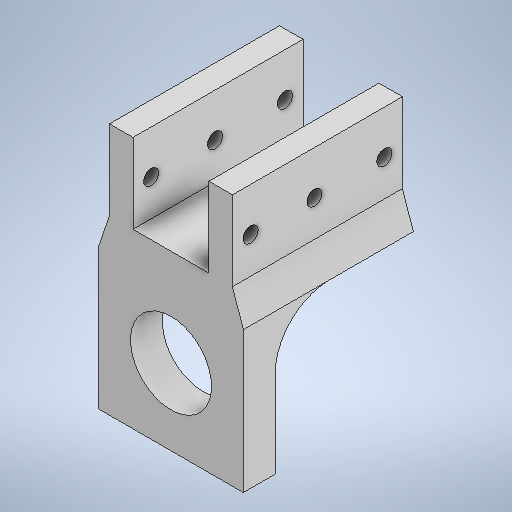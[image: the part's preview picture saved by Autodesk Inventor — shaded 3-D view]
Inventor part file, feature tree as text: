
AUTODESK INVENTOR PART (.ipt)
format: ipt  version: 2025.1 (Build 291241020, 241B)  size: 410,112 bytes
history: native  units: in
note: dims shown in document units (in); Inventor stores cm internally (conversion verified against a paired STEP export)
features: extrude x11, sketch x11, projected_geometry x11, fillet x1
ambient origin geometry x8: Origin, YZ Plane, XZ Plane, XY Plane, X Axis, Y Axis, Z Axis, Center Point
bodies: Solid1 (feature_tree)
feature tree (34):
  extrude  "Extrusion1"  Depth=2.0in
  extrude  "Extrusion3"  Depth=1.0in
  extrude  "Extrusion4"  Depth=0.35in TaperAngle=0.0deg
  extrude  "Extrusion5"  Depth=2.0in TaperAngle=0.0deg
  extrude  "Extrusion6"  Depth=1.05in
  extrude  "Extrusion7"  Depth=0.09in TaperAngle=0.0deg
  extrude  "Extrusion8"  Depth=1.465in TaperAngle=0.0deg
  extrude  "Extrusion9"  Depth=0.5in
  extrude  "Extrusion10"  Depth=0.25in
  extrude  "Extrusion11"  Depth=0.25in
  extrude  "Extrusion12"  TaperAngle=0.0deg  [1 undecoded]
  fillet  "Fillet5"  Radius=0.44in
  sketch  "Sketch1"  dims[d1=1.95in d2=2.0in]
  sketch  "Sketch3"  dims[d6=0.35in d7=1.0in]
  projected_geometry  "Projected Loop2"
  sketch  "Sketch5"  dims[d8=0.35in d9=0.35in d10=0.0in]
  projected_geometry  "Projected Loop3"
  sketch  "Sketch9"  dims[d13=1.12in d14=2.0in d15=0.0in]
  sketch  "Sketch11"  dims[d23=5.25in d24=0.0in d27=1.05in]
  projected_geometry  "Projected Loop8"
  projected_geometry  "Projected Loop9"
  sketch  "Sketch12"  dims[d28=1.6875in d29=0.0in d30=0.09in d31=0.0in]
  projected_geometry  "Projected Loop10"
  sketch  "Sketch13"  dims[d32=0.2225in d33=0.0in d34=1.465in d35=0.0in]
  sketch  "Sketch14"  dims[d36=1.84in d37=0.0in d39=0.5in]
  projected_geometry  "Projected Loop11"
  projected_geometry  "Projected Loop12"
  projected_geometry  "Projected Loop13"
  sketch  "Sketch15"  dims[d40=0.209in d41=0.25in]
  projected_geometry  "Projected Loop14"
  sketch  "Sketch16"  dims[d42=0.209in d43=0.25in]
  projected_geometry  "Projected Loop15"
  projected_geometry  "Projected Loop16"
  sketch  "Sketch17"  dims[d44=0.209in d46=0.0in d47=0.44in d51=1.12in d52=1.34in d53=1.7in d54=1.3375in d55=0.0in d56=0.1in d57=0.0in d58=1.0in d59=0.0in d60=0.75in]
note: 1 required parameter value undecoded (feature->parameter linkage not recoverable at this tier; creation-order binding heuristic only, values carry confidence <= 0.55)
